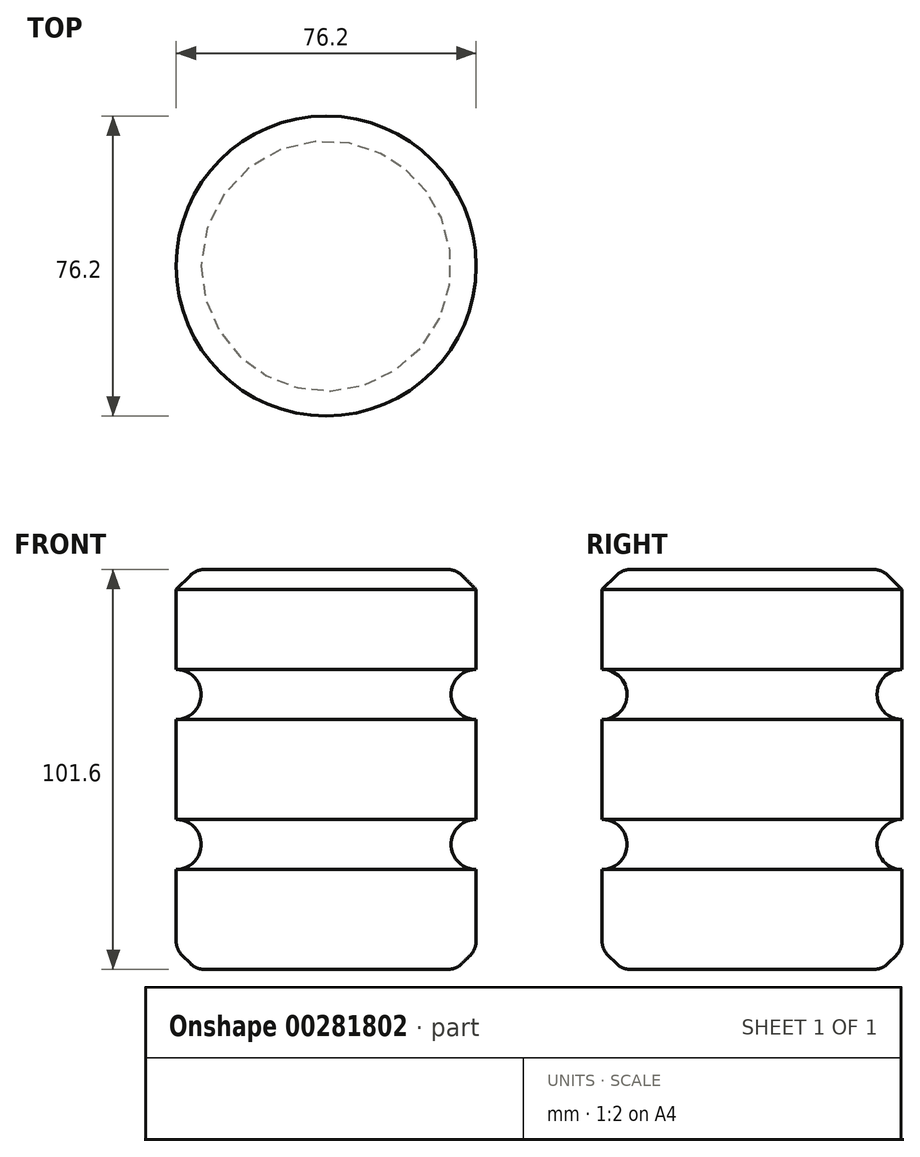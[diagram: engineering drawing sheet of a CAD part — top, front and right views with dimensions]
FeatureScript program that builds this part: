
annotation { "Feature Type Name" : "Feature", "Feature Type Description" : "" }
export const myFeature = defineFeature(function(context is Context, id is Id, definition is map)
    precondition{}
    {
        {
            var Q0;
            Q0=qCreatedBy(makeId("Front.planeOp"),FACE);
            var sketch = newSketch(context, id + "F0", { "sketchPlane" : qUnion([Q0])});
            skLineSegment(sketch, "E0.bottom", {"start": v(0, 0) * mm, "end": v(-38.1, 0) * mm});
            skLineSegment(sketch, "E0.top", {"start": v(0, 101.6) * mm, "end": v(-38.1, 101.6) * mm});
            skLineSegment(sketch, "E0.left", {"start": v(0, 0) * mm, "end": v(0, 25.4) * mm});
            skLineSegment(sketch, "E0.right", {"start": v(-38.1, 0) * mm, "end": v(-38.1, 101.6) * mm});
            skArc(sketch, "E1", {"start": v(0, 76.2) * mm, "mid": v(-6.35, 69.85) * mm, "end": v(0, 63.5) * mm});
            skArc(sketch, "E2", {"start": v(0, 38.1) * mm, "mid": v(-6.35, 31.75) * mm, "end": v(0, 25.4) * mm});
            skLineSegment(sketch, "E3.trimOffspring", {"start": v(0, 76.2) * mm, "end": v(0, 101.6) * mm});
            skLineSegment(sketch, "E4.trimOffspring", {"start": v(0, 38.1) * mm, "end": v(0, 63.5) * mm});
            skSolve(sketch);
        }
        {
            var Q0;
            Q0=makeQuery(id+"F0.imprint","IMPRINT",FACE,{"disambiguationData":[TD([[makeQuery(id+"F0.imprint","IMPRINT",EDGE,{"derivedFrom":sQuery(id+"F0.wireOp",EDGE,"E0.bottom")}),-1.0]])]});
            var Q1;
            Q1=sQuery(id+"F0.wireOp",EDGE,"E0.right");
            revolve(context, id + "F1", {"entities" : qUnion([Q0]), "axis" : qUnion([Q1]), "revolveType" : RevolveType.FULL});
        }
        {
            var Q0;
            Q0=makeQuery(id+"F1.opRevolve","SWEPT_EDGE",EDGE,{"disambiguationData":[OSD([sQuery(id+"F0.wireOp",EDGE,"E0.bottom"),sQuery(id+"F0.wireOp",EDGE,"E0.left")])]});
            chamfer(context, id + "F2", {"entities" : qUnion([Q0]), "width" : 5.08 * mm, "tangentPropagation" : true});
        }
        {
            var Q0;
            Q0=makeQuery(id+"F2.opChamfer","BLEND_FACE",FACE,{"disambiguationData":[OSD([sQuery(id+"F0.wireOp",EDGE,"E0.bottom"),sQuery(id+"F0.wireOp",EDGE,"E0.left")])]});
            fillet(context, id + "F3", {"entities" : qUnion([Q0]), "radius" : 5.08 * mm, "tangentPropagation" : true, "allowEdgeOverflow" : false});
        }
        {
            var Q0;
            Q0=makeQuery(id+"F1.opRevolve","SWEPT_FACE",FACE,{"disambiguationData":[OSD([sQuery(id+"F0.wireOp",EDGE,"E0.top")])]});
            chamfer(context, id + "F4", {"entities" : qUnion([Q0]), "width" : 5.08 * mm, "tangentPropagation" : true});
        }
        {
            var Q0;
            {var subQ0=sQuery(id+"F0.wireOp",EDGE,"E0.top");Q0=makeQuery(id+"F4.opChamfer","BLEND_EDGE",EDGE,{"blendedFrom":[makeQuery(id+"F1.opRevolve","SWEPT_EDGE",EDGE,{"disambiguationData":[OSD([subQ0,sQuery(id+"F0.wireOp",EDGE,"E3.trimOffspring")])]}),makeQuery(id+"F1.opRevolve","SWEPT_FACE",FACE,{"disambiguationData":[OSD([subQ0])]})],"blendedInto":[makeQuery(id+"F1.opRevolve","SWEPT_FACE",FACE,{"disambiguationData":[OSD([subQ0])]})]});}
            fillet(context, id + "F5", {"entities" : qUnion([Q0]), "radius" : 5.08 * mm, "tangentPropagation" : true, "allowEdgeOverflow" : false});
        }
    });
